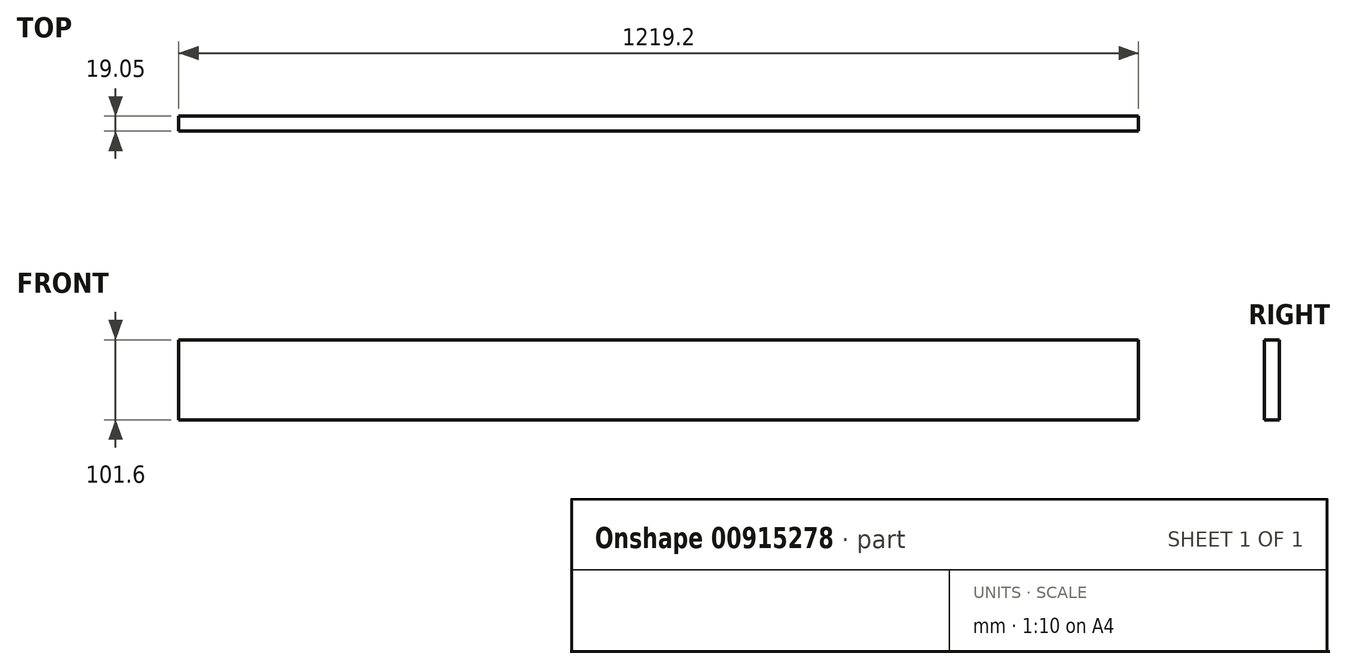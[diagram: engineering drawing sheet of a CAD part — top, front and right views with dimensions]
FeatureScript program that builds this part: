
annotation { "Feature Type Name" : "Feature", "Feature Type Description" : "" }
export const myFeature = defineFeature(function(context is Context, id is Id, definition is map)
    precondition{}
    {
        {
            var Q0;
            Q0=qCreatedBy(makeId("Front.planeOp"),FACE);
            var sketch = newSketch(context, id + "F0", { "sketchPlane" : qUnion([Q0])});
            skLineSegment(sketch, "E0.bottom", {"start": v(-609.6, 50.8) * mm, "end": v(609.6, 50.8) * mm});
            skLineSegment(sketch, "E0.top", {"start": v(-609.6, -50.8) * mm, "end": v(609.6, -50.8) * mm});
            skLineSegment(sketch, "E0.left", {"start": v(-609.6, 50.8) * mm, "end": v(-609.6, -50.8) * mm});
            skLineSegment(sketch, "E0.right", {"start": v(609.6, 50.8) * mm, "end": v(609.6, -50.8) * mm});
            skPoint(sketch, "E0.middle", {"position": v(0, 0) * mm});
            skSolve(sketch);
        }
        {
            var Q0;
            Q0=makeQuery(id+"F0.imprint","IMPRINT",FACE,{"disambiguationData":[TD([[makeQuery(id+"F0.imprint","IMPRINT",EDGE,{"derivedFrom":sQuery(id+"F0.wireOp",EDGE,"E0.bottom")}),-1.0]])]});
            extrude(context, id + "F1", {"entities" : qUnion([Q0]), "depth" : 19.05 * mm, "offsetDistance" : 25.4 * mm});
        }
    });
